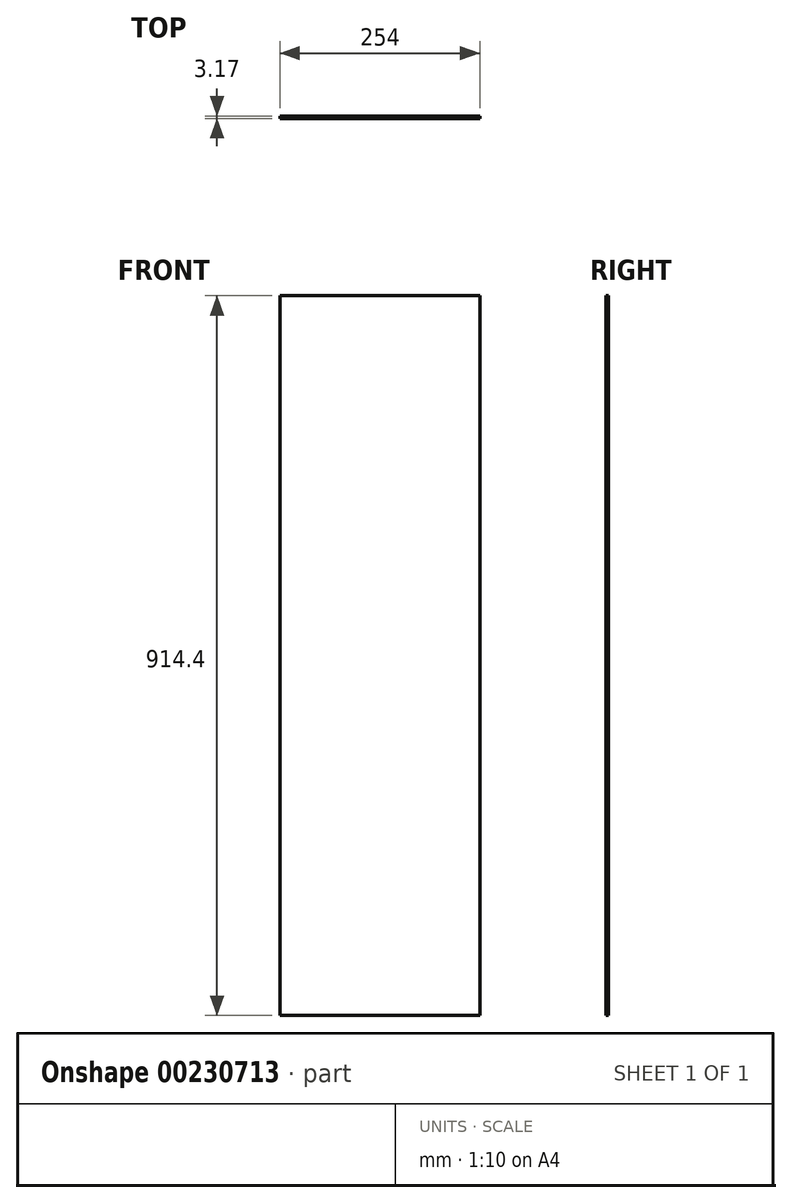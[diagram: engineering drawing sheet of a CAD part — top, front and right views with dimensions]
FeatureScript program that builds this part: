
annotation { "Feature Type Name" : "Feature", "Feature Type Description" : "" }
export const myFeature = defineFeature(function(context is Context, id is Id, definition is map)
    precondition{}
    {
        {
            var Q0;
            Q0=qCreatedBy(makeId("Front.planeOp"),FACE);
            var sketch = newSketch(context, id + "F0", { "sketchPlane" : qUnion([Q0])});
            skLineSegment(sketch, "E0.bottom", {"start": v(-129.65, 767.98) * mm, "end": v(124.35, 767.98) * mm});
            skLineSegment(sketch, "E0.top", {"start": v(-129.65, -146.42) * mm, "end": v(124.35, -146.42) * mm});
            skLineSegment(sketch, "E0.left", {"start": v(-129.65, 767.98) * mm, "end": v(-129.65, -146.42) * mm});
            skLineSegment(sketch, "E0.right", {"start": v(124.35, 767.98) * mm, "end": v(124.35, -146.42) * mm});
            skSolve(sketch);
        }
        {
            var Q0;
            Q0=makeQuery(id+"F0.imprint","IMPRINT",FACE,{"disambiguationData":[TD([[makeQuery(id+"F0.imprint","IMPRINT",EDGE,{"derivedFrom":sQuery(id+"F0.wireOp",EDGE,"E0.bottom")}),-1.0]])]});
            extrude(context, id + "F1", {"entities" : qUnion([Q0]), "depth" : 3.17 * mm});
        }
    });
